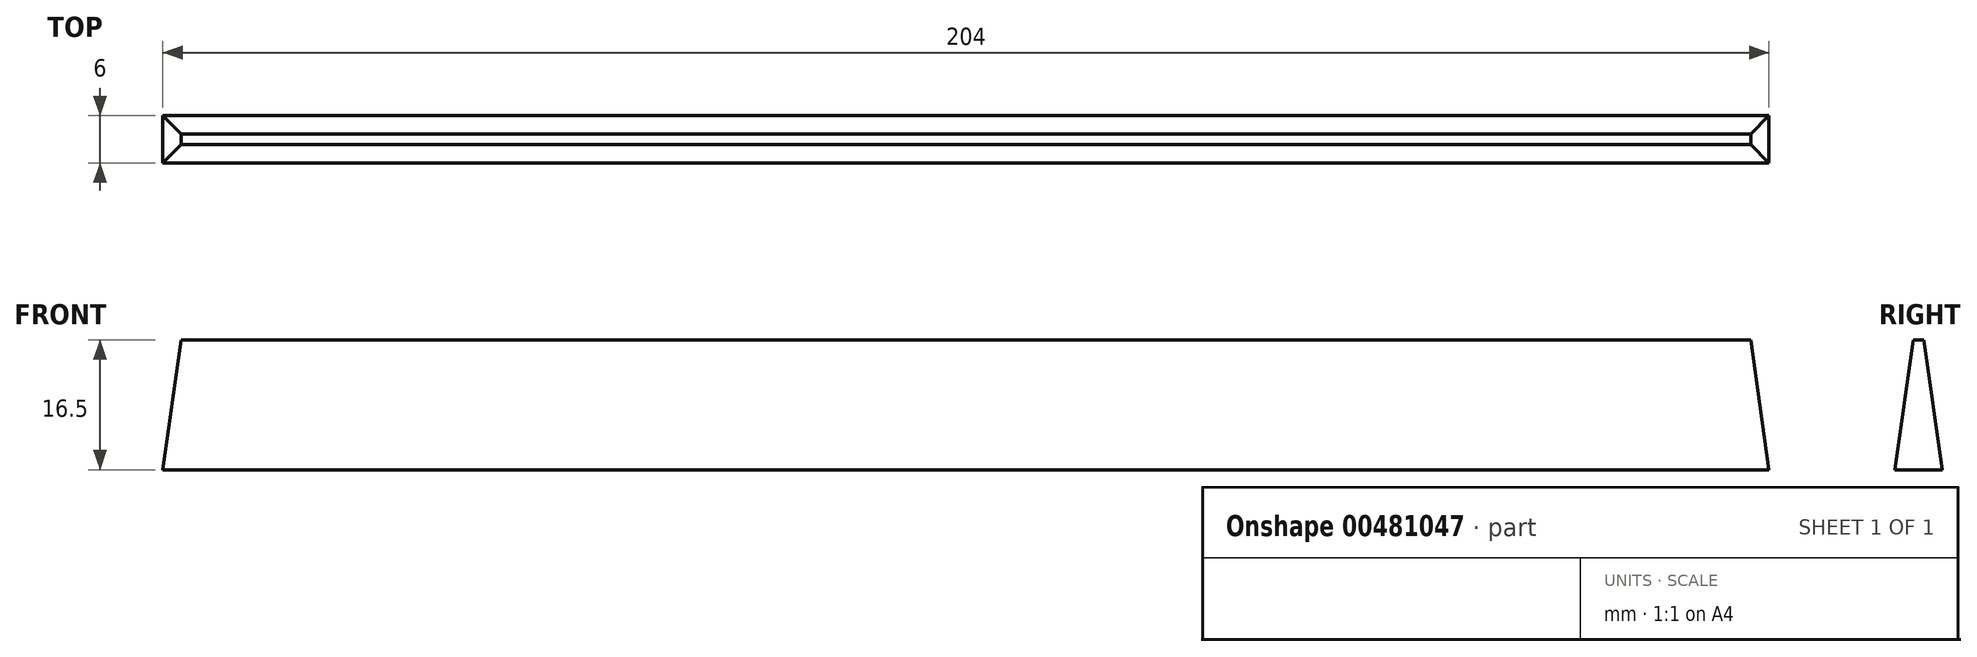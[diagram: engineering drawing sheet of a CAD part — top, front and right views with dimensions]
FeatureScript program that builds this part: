
annotation { "Feature Type Name" : "Feature", "Feature Type Description" : "" }
export const myFeature = defineFeature(function(context is Context, id is Id, definition is map)
    precondition{}
    {
        {
            var Q0;
            Q0=qCreatedBy(makeId("Top.planeOp"),FACE);
            var sketch = newSketch(context, id + "F0", { "sketchPlane" : qUnion([Q0])});
            skLineSegment(sketch, "E0.bottom", {"start": v(-97.1, 7.17) * mm, "end": v(106.9, 7.17) * mm});
            skLineSegment(sketch, "E0.top", {"start": v(-97.1, 1.17) * mm, "end": v(106.9, 1.17) * mm});
            skLineSegment(sketch, "E0.left", {"start": v(-97.1, 7.17) * mm, "end": v(-97.1, 1.17) * mm});
            skLineSegment(sketch, "E0.right", {"start": v(106.9, 7.17) * mm, "end": v(106.9, 1.17) * mm});
            skSolve(sketch);
        }
        {
            var Q0;
            Q0=makeQuery(id+"F0.imprint","IMPRINT",FACE,{"disambiguationData":[TD([[makeQuery(id+"F0.imprint","IMPRINT",EDGE,{"derivedFrom":sQuery(id+"F0.wireOp",EDGE,"E0.bottom")}),-1.0]])]});
            extrude(context, id + "F1", {"entities" : qUnion([Q0]), "depth" : 16.5 * mm, "hasDraft" : true, "draftAngle" : 8 * degree, "draftPullDirection" : true});
        }
    });
